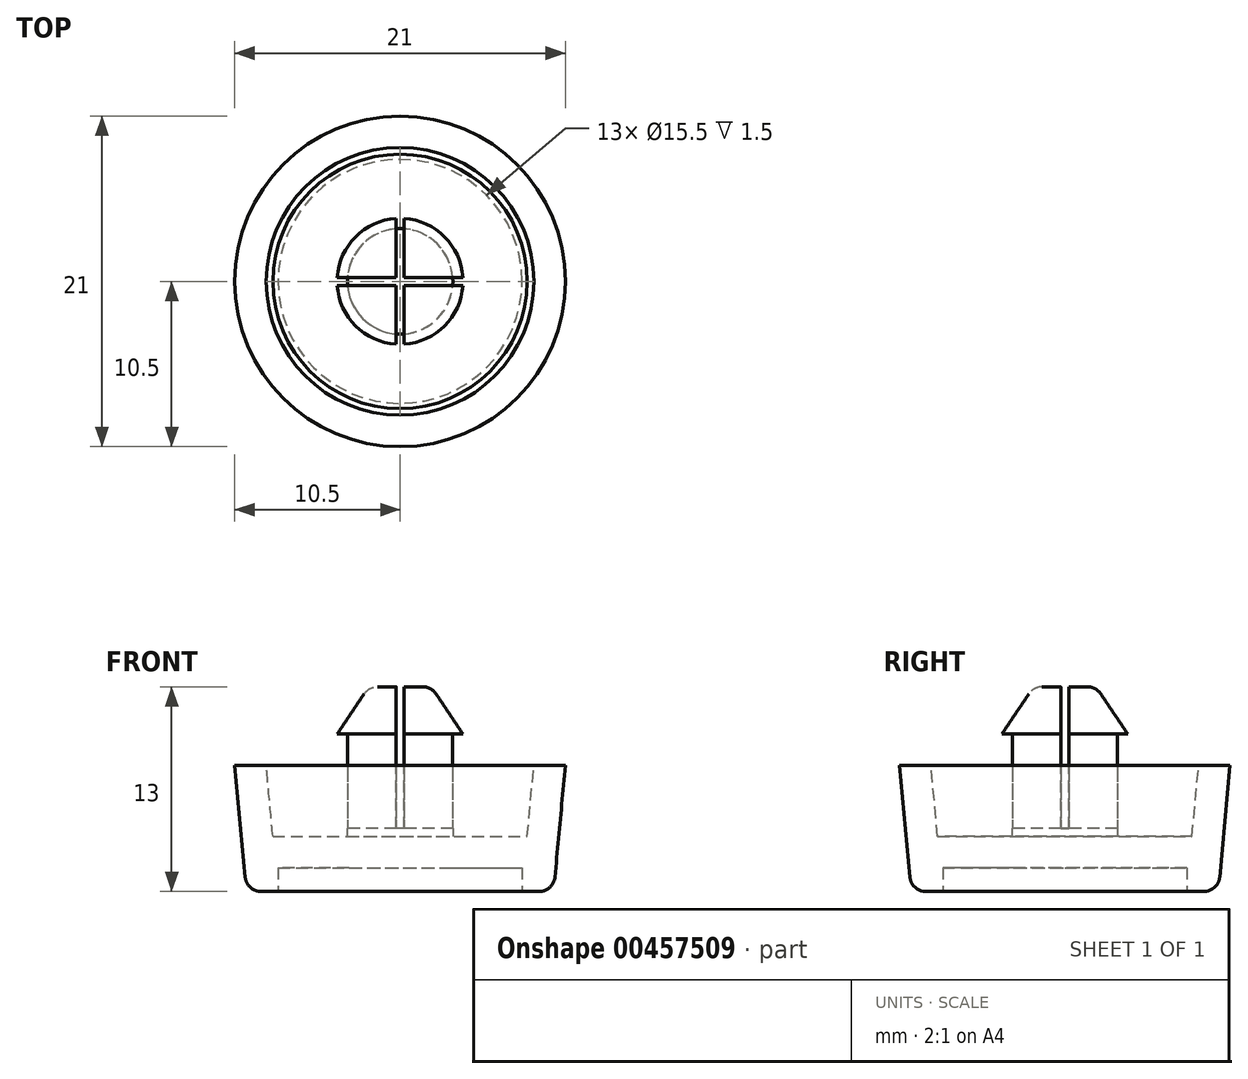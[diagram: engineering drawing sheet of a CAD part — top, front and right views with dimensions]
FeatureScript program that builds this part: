
annotation { "Feature Type Name" : "Feature", "Feature Type Description" : "" }
export const myFeature = defineFeature(function(context is Context, id is Id, definition is map)
    precondition{}
    {
        {
            var Q0;
            Q0=qCreatedBy(makeId("Front.planeOp"),FACE);
            var sketch = newSketch(context, id + "F0", { "sketchPlane" : qUnion([Q0])});
            skLineSegment(sketch, "E0", {"start": v(0, 26.63) * mm, "end": v(0, -30.3) * mm, "construction": true});
            skLineSegment(sketch, "E1", {"start": v(0, 0) * mm, "end": v(9.75, 0) * mm, "construction": true});
            skLineSegment(sketch, "E2", {"start": v(9.75, 0) * mm, "end": v(7.75, 0) * mm});
            skLineSegment(sketch, "E3", {"start": v(7.75, 0) * mm, "end": v(7.75, 1.5) * mm});
            skLineSegment(sketch, "E4", {"start": v(0, 0) * mm, "end": v(0, 8) * mm, "construction": true});
            skLineSegment(sketch, "E5", {"start": v(9.75, 0) * mm, "end": v(10.5, 8) * mm});
            skLineSegment(sketch, "E6", {"start": v(10.5, 8) * mm, "end": v(8.5, 8) * mm});
            skLineSegment(sketch, "E7", {"start": v(0, 1.5) * mm, "end": v(3.25, 1.5) * mm, "construction": true});
            skLineSegment(sketch, "E8", {"start": v(0, 8) * mm, "end": v(0, 5) * mm, "construction": true});
            skLineSegment(sketch, "E9", {"start": v(7.75, 1.5) * mm, "end": v(3.25, 1.5) * mm});
            skLineSegment(sketch, "E10", {"start": v(0, 1.5) * mm, "end": v(0, 3.5) * mm, "construction": true});
            skLineSegment(sketch, "E11", {"start": v(8.5, 8) * mm, "end": v(8.08, 3.5) * mm});
            skLineSegment(sketch, "E12", {"start": v(8.08, 3.5) * mm, "end": v(3.35, 3.5) * mm});
            skLineSegment(sketch, "E13", {"start": v(3.25, 1.5) * mm, "end": v(0, 1.5) * mm});
            skLineSegment(sketch, "E14", {"start": v(0, 1.5) * mm, "end": v(0, 8) * mm});
            skLineSegment(sketch, "E15", {"start": v(0, 0) * mm, "end": v(0, 13) * mm, "construction": true});
            skLineSegment(sketch, "E16", {"start": v(0, 13) * mm, "end": v(2, 13) * mm});
            skLineSegment(sketch, "E17", {"start": v(0, 13) * mm, "end": v(0, 10) * mm, "construction": true});
            skLineSegment(sketch, "E18", {"start": v(0, 10) * mm, "end": v(4, 10) * mm, "construction": true});
            skLineSegment(sketch, "E19", {"start": v(2, 13) * mm, "end": v(4, 10) * mm});
            skLineSegment(sketch, "E20", {"start": v(3.35, 3.5) * mm, "end": v(3.35, 10) * mm});
            skLineSegment(sketch, "E21", {"start": v(3.35, 10) * mm, "end": v(4, 10) * mm});
            skLineSegment(sketch, "E22", {"start": v(0, 1.5) * mm, "end": v(0, 13) * mm});
            skLineSegment(sketch, "E23", {"start": v(0, 8) * mm, "end": v(17.24, 8) * mm, "construction": true});
            skLineSegment(sketch, "E24", {"start": v(0, 3.5) * mm, "end": v(19.07, 3.5) * mm, "construction": true});
            skSolve(sketch);
        }
        {
            var Q0;
            Q0=makeQuery(id+"F0.imprint","IMPRINT",FACE,{"disambiguationData":[TD([[makeQuery(id+"F0.imprint","IMPRINT",EDGE,{"derivedFrom":sQuery(id+"F0.wireOp",EDGE,"E2")}),-1.0]])]});
            var Q1;
            Q1=sQuery(id+"F0.wireOp",EDGE,"E4");
            revolve(context, id + "F1", {"entities" : qUnion([Q0]), "axis" : qUnion([Q1]), "revolveType" : RevolveType.FULL});
        }
        {
            var Q0;
            Q0=makeQuery(id+"F1.opRevolve","SWEPT_FACE",FACE,{"disambiguationData":[OSD([sQuery(id+"F0.wireOp",EDGE,"E16")])]});
            var sketch = newSketch(context, id + "F2", { "sketchPlane" : qUnion([Q0])});
            skLineSegment(sketch, "E25.bottom", {"start": v(0.25, 4) * mm, "end": v(-0.25, 4) * mm});
            skLineSegment(sketch, "E25.top", {"start": v(0.25, -4) * mm, "end": v(-0.25, -4) * mm});
            skLineSegment(sketch, "E25.left", {"start": v(0.25, 4) * mm, "end": v(0.25, -4) * mm});
            skLineSegment(sketch, "E25.right", {"start": v(-0.25, 4) * mm, "end": v(-0.25, -4) * mm});
            skPoint(sketch, "E25.middle", {"position": v(0, 0) * mm});
            skLineSegment(sketch, "E26.bottom", {"start": v(4, -0.25) * mm, "end": v(-4, -0.25) * mm});
            skLineSegment(sketch, "E26.top", {"start": v(4, 0.25) * mm, "end": v(-4, 0.25) * mm});
            skLineSegment(sketch, "E26.left", {"start": v(4, -0.25) * mm, "end": v(4, 0.25) * mm});
            skLineSegment(sketch, "E26.right", {"start": v(-4, -0.25) * mm, "end": v(-4, 0.25) * mm});
            skSolve(sketch);
        }
        {
            var Q0;
            {var subQ0=sQuery(id+"F2.wireOp",EDGE,"E26.right");Q0=makeQuery(id+"F2.imprint","IMPRINT",FACE,{"disambiguationData":[TD([[makeQuery(id+"F2.imprint","IMPRINT",EDGE,{"derivedFrom":subQ0}),-1.0]])]});}
            var Q1;
            {var subQ0=sQuery(id+"F2.wireOp",EDGE,"E26.top");var subQ1=sQuery(id+"F2.wireOp",EDGE,"E25.right");var subQ2=makeQuery(id+"F2.imprint","INTERSECT",VERTEX,{"derivedFrom":[subQ1,subQ0]});Q1=makeQuery(id+"F2.imprint","IMPRINT",FACE,{"disambiguationData":[TD([[makeQuery(id+"F2.imprint","IMPRINT",EDGE,{"disambiguationData":[TD([[subQ2,-1.0]])],"derivedFrom":subQ1}),-1.0]])]});}
            var Q2;
            {var subQ0=sQuery(id+"F2.wireOp",EDGE,"E26.top");var subQ1=sQuery(id+"F2.wireOp",EDGE,"E25.left");var subQ2=makeQuery(id+"F2.imprint","INTERSECT",VERTEX,{"derivedFrom":[subQ1,subQ0]});Q2=makeQuery(id+"F2.imprint","IMPRINT",FACE,{"disambiguationData":[TD([[makeQuery(id+"F2.imprint","IMPRINT",EDGE,{"disambiguationData":[TD([[subQ2,-1.0]])],"derivedFrom":subQ1}),-1.0]])]});}
            var Q3;
            {var subQ0=sQuery(id+"F2.wireOp",EDGE,"E26.top");var subQ1=sQuery(id+"F2.wireOp",EDGE,"E25.left");var subQ2=makeQuery(id+"F2.imprint","INTERSECT",VERTEX,{"derivedFrom":[subQ1,subQ0]});Q3=makeQuery(id+"F2.imprint","IMPRINT",FACE,{"disambiguationData":[TD([[makeQuery(id+"F2.imprint","IMPRINT",EDGE,{"disambiguationData":[TD([[subQ2,-1.0]])],"derivedFrom":subQ1}),1.0]])]});}
            var Q4;
            {var subQ0=sQuery(id+"F2.wireOp",EDGE,"E26.left");Q4=makeQuery(id+"F2.imprint","IMPRINT",FACE,{"disambiguationData":[TD([[makeQuery(id+"F2.imprint","IMPRINT",EDGE,{"derivedFrom":subQ0}),1.0]])]});}
            var Q5;
            {var subQ0=sQuery(id+"F2.wireOp",EDGE,"E25.bottom");Q5=makeQuery(id+"F2.imprint","IMPRINT",FACE,{"disambiguationData":[TD([[makeQuery(id+"F2.imprint","IMPRINT",EDGE,{"derivedFrom":subQ0}),1.0]])]});}
            var Q6;
            {var subQ0=sQuery(id+"F2.wireOp",EDGE,"E26.top");var subQ1=sQuery(id+"F2.wireOp",EDGE,"E25.left");var subQ2=makeQuery(id+"F2.imprint","INTERSECT",VERTEX,{"derivedFrom":[subQ1,subQ0]});Q6=makeQuery(id+"F2.imprint","IMPRINT",FACE,{"disambiguationData":[TD([[makeQuery(id+"F2.imprint","IMPRINT",EDGE,{"disambiguationData":[TD([[subQ2,-1.0]])],"derivedFrom":subQ0}),-1.0]])]});}
            var Q7;
            {var subQ0=sQuery(id+"F2.wireOp",EDGE,"E26.bottom");var subQ1=sQuery(id+"F2.wireOp",EDGE,"E25.left");var subQ2=makeQuery(id+"F2.imprint","INTERSECT",VERTEX,{"derivedFrom":[subQ1,subQ0]});Q7=makeQuery(id+"F2.imprint","IMPRINT",FACE,{"disambiguationData":[TD([[makeQuery(id+"F2.imprint","IMPRINT",EDGE,{"disambiguationData":[TD([[subQ2,-1.0]])],"derivedFrom":subQ0}),1.0]])]});}
            var Q8;
            {var subQ0=sQuery(id+"F2.wireOp",EDGE,"E25.top");Q8=makeQuery(id+"F2.imprint","IMPRINT",FACE,{"disambiguationData":[TD([[makeQuery(id+"F2.imprint","IMPRINT",EDGE,{"derivedFrom":subQ0}),-1.0]])]});}
            extrude(context, id + "F3", {"entities" : qUnion([Q0, Q1, Q2, Q3, Q4, Q5, Q6, Q7, Q8]), "operationType" : NewBodyOperationType.REMOVE, "oppositeDirection" : true, "depth" : 9 * mm});
        }
        {
            var Q0;
            Q0=makeQuery(id+"F1.opRevolve","SWEPT_EDGE",EDGE,{"disambiguationData":[OSD([sQuery(id+"F0.wireOp",EDGE,"E2"),sQuery(id+"F0.wireOp",EDGE,"E5")])]});
            fillet(context, id + "F4", {"entities" : qUnion([Q0]), "radius" : 1 * mm, "tangentPropagation" : true, "allowEdgeOverflow" : false});
        }
        {
            var Q0;
            {var subQ0=sQuery(id+"F0.wireOp",EDGE,"E16");var subQ1=sQuery(id+"F0.wireOp",EDGE,"E19");var subQ2=sQuery(id+"F2.wireOp",EDGE,"E25.right");var subQ3=makeQuery(id+"F1.opRevolve","SWEPT_EDGE",EDGE,{"disambiguationData":[OSD([subQ0,subQ1])]});var subQ5=sQuery(id+"F2.wireOp",EDGE,"E26.bottom");var subQ6=makeQuery(id+"F2.imprint","INTERSECT",VERTEX,{"derivedFrom":[subQ2,subQ5]});Q0=makeQuery(id+"F3.boolean.opBoolean","SPLIT",EDGE,{"disambiguationData":[TD([makeQuery(id+"F3.opExtrude","SWEPT_FACE",FACE,{"disambiguationData":[OSD([subQ2]),TDD([makeQuery(id+"F2.imprint","IMPRINT",EDGE,{"disambiguationData":[TD([[subQ6,-1.0]])],"derivedFrom":subQ2}),makeQuery(id+"F2.imprint","IMPRINT",EDGE,{"disambiguationData":[TD([[makeQuery(id+"F2.imprint","INTERSECT",VERTEX,{"derivedFrom":[sQuery(id+"F2.wireOp",EDGE,"E25.top"),subQ2]}),1.0]])],"derivedFrom":subQ2})])]})])],"derivedFrom":subQ3});}
            var Q1;
            {var subQ0=sQuery(id+"F0.wireOp",EDGE,"E16");var subQ1=sQuery(id+"F2.wireOp",EDGE,"E25.left");var subQ2=sQuery(id+"F0.wireOp",EDGE,"E19");var subQ3=makeQuery(id+"F1.opRevolve","SWEPT_EDGE",EDGE,{"disambiguationData":[OSD([subQ0,subQ2])]});var subQ5=sQuery(id+"F2.wireOp",EDGE,"E26.bottom");var subQ6=makeQuery(id+"F2.imprint","INTERSECT",VERTEX,{"derivedFrom":[subQ1,subQ5]});Q1=makeQuery(id+"F3.boolean.opBoolean","SPLIT",EDGE,{"disambiguationData":[TD([makeQuery(id+"F3.opExtrude","SWEPT_FACE",FACE,{"disambiguationData":[OSD([subQ1]),TDD([makeQuery(id+"F2.imprint","IMPRINT",EDGE,{"disambiguationData":[TD([[subQ6,-1.0]])],"derivedFrom":subQ1}),makeQuery(id+"F2.imprint","IMPRINT",EDGE,{"disambiguationData":[TD([[makeQuery(id+"F2.imprint","INTERSECT",VERTEX,{"derivedFrom":[sQuery(id+"F2.wireOp",EDGE,"E25.top"),subQ1]}),1.0]])],"derivedFrom":subQ1})])]})])],"derivedFrom":subQ3});}
            var Q2;
            {var subQ0=sQuery(id+"F0.wireOp",EDGE,"E16");var subQ1=sQuery(id+"F2.wireOp",EDGE,"E26.top");var subQ2=sQuery(id+"F2.wireOp",EDGE,"E25.left");var subQ3=makeQuery(id+"F2.imprint","INTERSECT",VERTEX,{"derivedFrom":[subQ2,subQ1]});var subQ4=sQuery(id+"F0.wireOp",EDGE,"E19");var subQ5=makeQuery(id+"F1.opRevolve","SWEPT_EDGE",EDGE,{"disambiguationData":[OSD([subQ0,subQ4])]});Q2=makeQuery(id+"F3.boolean.opBoolean","SPLIT",EDGE,{"disambiguationData":[TD([makeQuery(id+"F3.opExtrude","SWEPT_FACE",FACE,{"disambiguationData":[OSD([subQ2]),TDD([makeQuery(id+"F2.imprint","IMPRINT",EDGE,{"disambiguationData":[TD([[makeQuery(id+"F2.imprint","INTERSECT",VERTEX,{"derivedFrom":[sQuery(id+"F2.wireOp",EDGE,"E25.bottom"),subQ2]}),-1.0]])],"derivedFrom":subQ2}),makeQuery(id+"F2.imprint","IMPRINT",EDGE,{"disambiguationData":[TD([[subQ3,1.0]])],"derivedFrom":subQ2})])]})])],"derivedFrom":subQ5});}
            var Q3;
            {var subQ0=sQuery(id+"F0.wireOp",EDGE,"E16");var subQ1=sQuery(id+"F0.wireOp",EDGE,"E19");var subQ2=sQuery(id+"F2.wireOp",EDGE,"E26.top");var subQ3=sQuery(id+"F2.wireOp",EDGE,"E25.right");var subQ4=makeQuery(id+"F2.imprint","INTERSECT",VERTEX,{"derivedFrom":[subQ3,subQ2]});var subQ5=makeQuery(id+"F1.opRevolve","SWEPT_EDGE",EDGE,{"disambiguationData":[OSD([subQ0,subQ1])]});Q3=makeQuery(id+"F3.boolean.opBoolean","SPLIT",EDGE,{"disambiguationData":[TD([makeQuery(id+"F3.opExtrude","SWEPT_FACE",FACE,{"disambiguationData":[OSD([subQ3]),TDD([makeQuery(id+"F2.imprint","IMPRINT",EDGE,{"disambiguationData":[TD([[makeQuery(id+"F2.imprint","INTERSECT",VERTEX,{"derivedFrom":[sQuery(id+"F2.wireOp",EDGE,"E25.bottom"),subQ3]}),-1.0]])],"derivedFrom":subQ3}),makeQuery(id+"F2.imprint","IMPRINT",EDGE,{"disambiguationData":[TD([[subQ4,1.0]])],"derivedFrom":subQ3})])]})])],"derivedFrom":subQ5});}
            fillet(context, id + "F5", {"entities" : qUnion([Q0, Q1, Q2, Q3]), "radius" : 1 * mm, "tangentPropagation" : true, "allowEdgeOverflow" : false});
        }
    });
